# Revit family: Haworth_BeHold_PersonalStorageTower_SideBookcase_15Wide
name_source: partatom
category: Furniture Systems
revit_build: Autodesk Revit 2018 (Build: 20170223_1515(x64)
units: mm (PartAtom-declared; Revit-internal decimal feet)

## family parameters
Always vertical = Yes
Cut with Voids When Loaded = No
OmniClass Number = 23.40.70.14.64.21
OmniClass Title = Systems Furniture
Part Type = Normal
Room Calculation Point = No
Round Connector Dimension = Use Diameter
Shared = No
Work Plane-Based = No

## types (8) — shared parameters
Actual Width = 15"
Assembly Code = E2020200
Back Case Back Control = 0"
Blade Pull = No
Blade Pull Length = 14 13/16"
Bottom Case Offset = 1/2"
Bottom Drawer Offset = 1 3/8"
Case Thickness = 3/4"
Classic Pull = No
Classic Pull Length = 7 1/2"
Cresent Pull = No
Custom Size = No
Description = Haworth - Be_Hold - Personal Storage Tower - Side Bookcase
Drawer Width = 14 7/8"
Glide Finish = Haworth _ Polymer _ Slate
Linear Pull = No
Linear Pull Length = 7 1/2"
Manufacturer = Haworth
Max. Depth = 30"
Max. Height = 65"
Max. Width = 15"
Min. Depth = 18"
Min. Height = 41"
Min. Width = 15"
Model = Haworth Be_Hold
Revision Number = 1
Shelf 1 Offset = 27 3/4"
Size = Verify Final Dim. w/ Haworth
Standard Depths = 18, 24, 30 in.
Standard Heights = 41, 49, 57, 65 in.
Storage Height = 28"
Sustainability Info = https://www.haworth.com
Top Case Back Control = 0"
Top Thickness = 3/4"
Total Drawer Height = 26 1/2"
URL = www.haworth.com
URL - Product = https://www.haworth.com
Warranty = http://www.haworth.com
Wing Pull = Yes
Wing Pull Length = 8 5/16"
With Lock = Yes

## per-type parameters (varying)
| type | 3 Drawer Control | Actual Depth | Actual Height | Back Case Side Control | Bottom Drawer Height | Box Box File | Depth | Distance Between Drawer | File File | Height | Inset Style | Middle Drawer Height | Proud Style | Shelf 2 Control | Shelf 2 Offset | Side Case Back Control | Top Drawer Height |
| B/B/F - 30d 65h - Inset Back | Yes | 30" | 65" | 3/4" | 13 1/8" | Yes | 30" | 1/4" | No | 65" | Yes | 6 9/16" | No | Yes | 49" | 0" | 6 9/16" |
| B/B/F - 24d 57h - Inset Back | Yes | 24" | 57" | 3/4" | 13 1/8" | Yes | 24" | 1/4" | No | 57" | Yes | 6 9/16" | No | Yes | 41" | 0" | 6 9/16" |
| B/B/F - 24d 49h - Inset Back | Yes | 24" | 49" | 3/4" | 13 1/8" | Yes | 24" | 1/4" | No | 49" | Yes | 6 9/16" | No | Yes | 32 5/16" | 0" | 6 9/16" |
| B/B/F - 18d 41h - Inset Back | Yes | 18" | 41" | 3/4" | 13 1/8" | Yes | 18" | 1/4" | No | 41" | Yes | 6 9/16" | No | No | 32 5/16" | 0" | 6 9/16" |
| F/F - 30d 65h - Proud Back | No | 30" | 65" | 0" | 13 3/16" | No | 30" | 1/8" | Yes | 65" | No | 6 19/32" | Yes | Yes | 49" | 3/4" | 13 3/16" |
| F/F - 24d 57h - Proud Back | No | 24" | 57" | 0" | 13 3/16" | No | 24" | 1/8" | Yes | 57" | No | 6 19/32" | Yes | Yes | 41" | 3/4" | 13 3/16" |
| F/F - 24d 49h - Proud Back | No | 24" | 49" | 0" | 13 3/16" | No | 24" | 1/8" | Yes | 49" | No | 6 19/32" | Yes | Yes | 32 5/16" | 3/4" | 13 3/16" |
| F/F - 18d 41h - Proud Back | No | 18" | 41" | 0" | 13 3/16" | No | 18" | 1/8" | Yes | 41" | No | 6 19/32" | Yes | No | 32 5/16" | 3/4" | 13 3/16" |

## geometry (parser evidence)
native form markers: Sweep x5
no freeform markers — native parametric forms only
